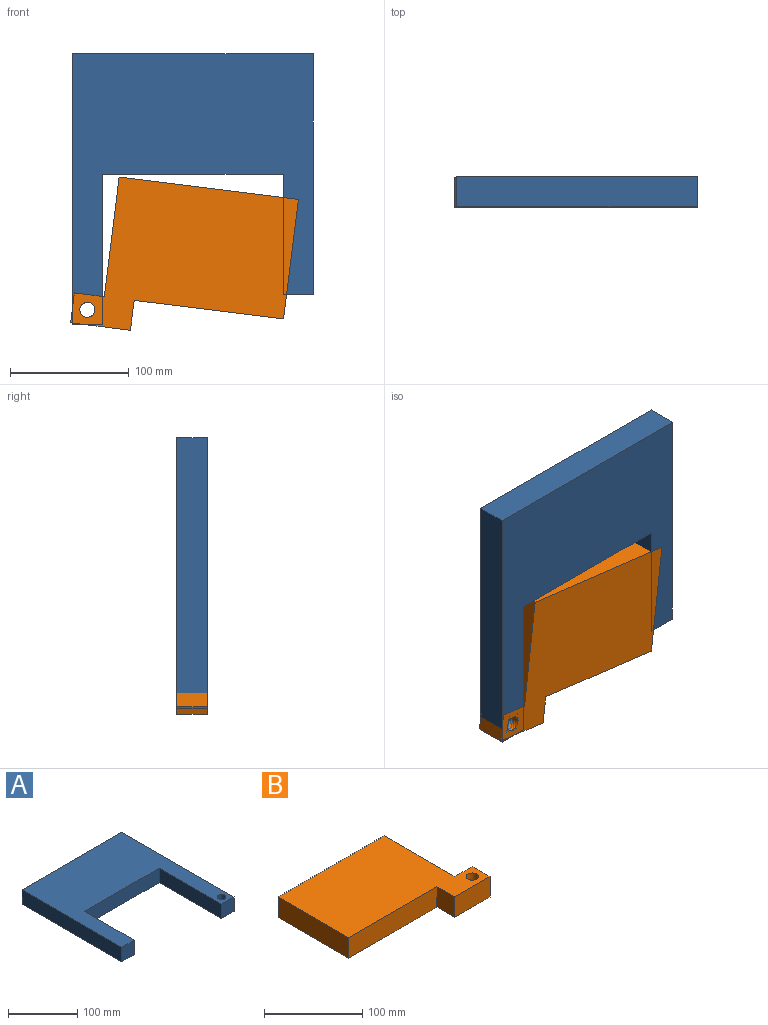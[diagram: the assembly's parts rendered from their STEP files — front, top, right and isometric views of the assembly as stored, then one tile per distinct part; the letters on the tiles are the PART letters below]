
ASSEMBLY  parts=2 mates=1
PART A: 11 faces, bbox 203.2x228.6x25.4 mm
  f0: plane 25.4x25.4mm, normal (0,-1,0), area 645.2mm2, adj f1,f6,f7,f8
  f1: plane 101.6x25.4mm, normal (1,0,0), area 2580.6mm2, adj f0,f2,f7,f8
  f2: plane 152.4x25.4mm, normal (0,-1,0), area 3871mm2, adj f1,f3,f7,f8
  f3: plane 127x25.4mm, normal (-1,0,0), area 3225.8mm2, adj f2,f7,f8,f9
  f4: plane 228.6x25.4mm, normal (1,0,0), area 5806.4mm2, adj f5,f7,f8,f9
  f5: plane 203.2x25.4mm, normal (0,1,0), area 5161.3mm2, adj f4,f6,f7,f8
  f6: plane 203.2x25.4mm, normal (-1,0,0), area 5161.3mm2, adj f0,f5,f7,f8
  f7: plane 228.6x203.2mm, normal (0,0,1), area 26324.9mm2, adj f0,f1,f2,f3,f4,f5,f6,f9
  f8: plane 228.6x203.2mm, normal (0,0,-1), area 26324.9mm2, adj f0,f1,f2,f3,f4,f5,f6,f9
  f9: plane 25.4x25.4mm, normal (0,-1,0), area 645.2mm2, adj f3,f4,f7,f8
  f10: cylinder r=6.35mm len=25.4mm, axis (0,0,1), area 1013.4mm2, adj f7,f8
PART B: 11 faces, bbox 177.8x127x25.4 mm
  f0: plane 127x25.4mm, normal (0,-1,0), area 3225.8mm2, adj f3,f4,f5,f6
  f1: plane 101.6x25.4mm, normal (1,0,0), area 2580.6mm2, adj f2,f4,f5,f8
  f2: plane 152.4x25.4mm, normal (0,1,0), area 3871mm2, adj f1,f3,f4,f5
  f3: plane 101.6x25.4mm, normal (-1,0,0), area 2580.6mm2, adj f0,f2,f4,f5
  f4: plane 177.8x127mm, normal (0,0,1), area 16647.5mm2, adj f0,f1,f2,f3,f6,f7,f8,f9
  f5: plane 177.8x127mm, normal (0,0,-1), area 16647.5mm2, adj f0,f1,f2,f3,f6,f7,f8,f9
  f6: plane 25.4x25.4mm, normal (-1,0,0), area 645.2mm2, adj f0,f4,f5,f7
  f7: plane 50.8x25.4mm, normal (0,-1,0), area 1290.3mm2, adj f4,f5,f6,f9
  f8: plane 25.4x25.4mm, normal (0,1,0), area 645.2mm2, adj f1,f4,f5,f9
  f9: plane 25.4x25.4mm, normal (1,0,0), area 645.2mm2, adj f4,f5,f7,f8
  f10: cylinder r=6.35mm len=25.4mm, axis (0,0,1), area 1013.4mm2, adj f4,f5
PLACE A rot(axis=(0,0.71,0.71),180deg) t=(1.75,-25.4,-27.63)mm
PLACE B rot(axis=(-0.04,-0.71,-0.71),175deg) t=(8.91,-25.4,-89.88)mm
MATE revolute A.f10 <-> B.f10  axis (0,1,0) through (-87.15,0,-141.93)mm
